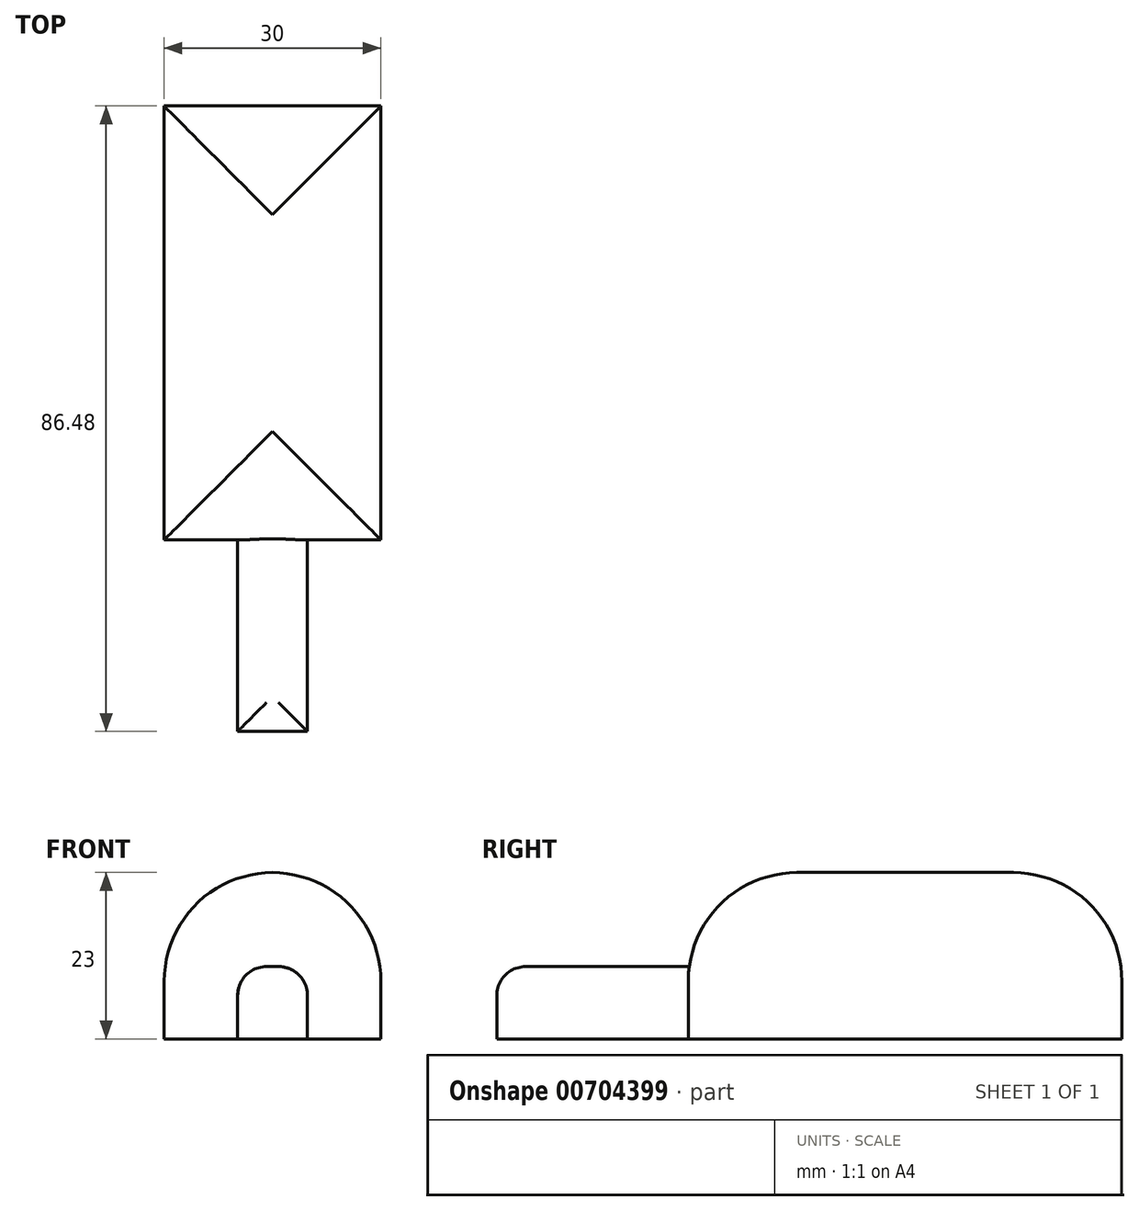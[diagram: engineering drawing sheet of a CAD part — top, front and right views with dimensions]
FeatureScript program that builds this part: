
annotation { "Feature Type Name" : "Feature", "Feature Type Description" : "" }
export const myFeature = defineFeature(function(context is Context, id is Id, definition is map)
    precondition{}
    {
        {
            var Q0;
            Q0=qCreatedBy(makeId("Top.planeOp"),FACE);
            var sketch = newSketch(context, id + "F0", { "sketchPlane" : qUnion([Q0])});
            skLineSegment(sketch, "E0.bottom", {"start": v(-15, 30) * mm, "end": v(15, 30) * mm});
            skLineSegment(sketch, "E0.top", {"start": v(-15, -30) * mm, "end": v(15, -30) * mm});
            skLineSegment(sketch, "E0.left", {"start": v(-15, 30) * mm, "end": v(-15, -30) * mm});
            skLineSegment(sketch, "E0.right", {"start": v(15, 30) * mm, "end": v(15, -30) * mm});
            skPoint(sketch, "E0.middle", {"position": v(0, 0) * mm});
            skSolve(sketch);
        }
        {
            var Q0;
            Q0=makeQuery(id+"F0.imprint","IMPRINT",FACE,{"disambiguationData":[TD([[makeQuery(id+"F0.imprint","IMPRINT",EDGE,{"derivedFrom":sQuery(id+"F0.wireOp",EDGE,"E0.bottom")}),-1.0]])]});
            var sketch = newSketch(context, id + "F1", { "sketchPlane" : qUnion([Q0])});
            skLineSegment(sketch, "E1", {"start": v(-4.83, -29.9) * mm, "end": v(-4.83, -56.48) * mm});
            skLineSegment(sketch, "E2", {"start": v(-4.83, -56.48) * mm, "end": v(0, -56.48) * mm});
            skLineSegment(sketch, "E3", {"start": v(-4.83, -29.9) * mm, "end": v(0, -29.9) * mm});
            skLineSegment(sketch, "E4.MirrorCS", {"start": v(4.83, -29.9) * mm, "end": v(0, -29.9) * mm});
            skLineSegment(sketch, "E5.MirrorCS", {"start": v(4.83, -29.9) * mm, "end": v(4.83, -56.48) * mm});
            skLineSegment(sketch, "E6.MirrorCS", {"start": v(4.83, -56.48) * mm, "end": v(0, -56.48) * mm});
            skSolve(sketch);
        }
        {
            var Q0;
            Q0=makeQuery(id+"F0.imprint","IMPRINT",FACE,{"disambiguationData":[TD([[makeQuery(id+"F0.imprint","IMPRINT",EDGE,{"derivedFrom":sQuery(id+"F0.wireOp",EDGE,"E0.bottom")}),-1.0]])]});
            extrude(context, id + "F2", {"entities" : qUnion([Q0]), "depth" : 23 * mm, "offsetDistance" : 25 * mm});
        }
        {
            var Q0;
            {var subQ1=sQuery(id+"F1.wireOp",EDGE,"E2");Q0=makeQuery(id+"F1.imprint","IMPRINT",FACE,{"disambiguationData":[TD([[makeQuery(id+"F1.imprint","IMPRINT",EDGE,{"derivedFrom":subQ1}),1.0]])]});}
            extrude(context, id + "F3", {"entities" : qUnion([Q0]), "operationType" : NewBodyOperationType.ADD, "depth" : 10 * mm, "offsetDistance" : 25 * mm});
        }
        {
            var Q0;
            Q0=makeQuery(id+"F2.opExtrude","CAP_EDGE",EDGE,{"disambiguationData":[OSD([sQuery(id+"F0.wireOp",EDGE,"E0.left")])],"isStart":false});
            var Q1;
            Q1=makeQuery(id+"F2.opExtrude","CAP_EDGE",EDGE,{"disambiguationData":[OSD([sQuery(id+"F0.wireOp",EDGE,"E0.top")])],"isStart":false});
            var Q2;
            Q2=makeQuery(id+"F2.opExtrude","CAP_EDGE",EDGE,{"disambiguationData":[OSD([sQuery(id+"F0.wireOp",EDGE,"E0.right")])],"isStart":false});
            var Q3;
            Q3=makeQuery(id+"F2.opExtrude","CAP_EDGE",EDGE,{"disambiguationData":[OSD([sQuery(id+"F0.wireOp",EDGE,"E0.bottom")])],"isStart":false});
            fillet(context, id + "F4", {"entities" : qUnion([Q0, Q1, Q2, Q3]), "radius" : 15 * mm, "tangentPropagation" : true, "allowEdgeOverflow" : false});
        }
        {
            var Q0;
            Q0=makeQuery(id+"F3.opExtrude","CAP_EDGE",EDGE,{"disambiguationData":[OSD([sQuery(id+"F1.wireOp",EDGE,"E1")])],"isStart":false});
            var Q1;
            Q1=makeQuery(id+"F3.opExtrude","CAP_EDGE",EDGE,{"disambiguationData":[OSD([sQuery(id+"F1.wireOp",EDGE,"E5.MirrorCS")])],"isStart":false});
            var Q2;
            Q2=makeQuery(id+"F3.opExtrude","CAP_EDGE",EDGE,{"disambiguationData":[OSD([sQuery(id+"F1.wireOp",EDGE,"E2"),sQuery(id+"F1.wireOp",EDGE,"E6.MirrorCS")])],"isStart":false});
            fillet(context, id + "F5", {"entities" : qUnion([Q0, Q1, Q2]), "radius" : 4 * mm, "tangentPropagation" : true, "allowEdgeOverflow" : false});
        }
    });
